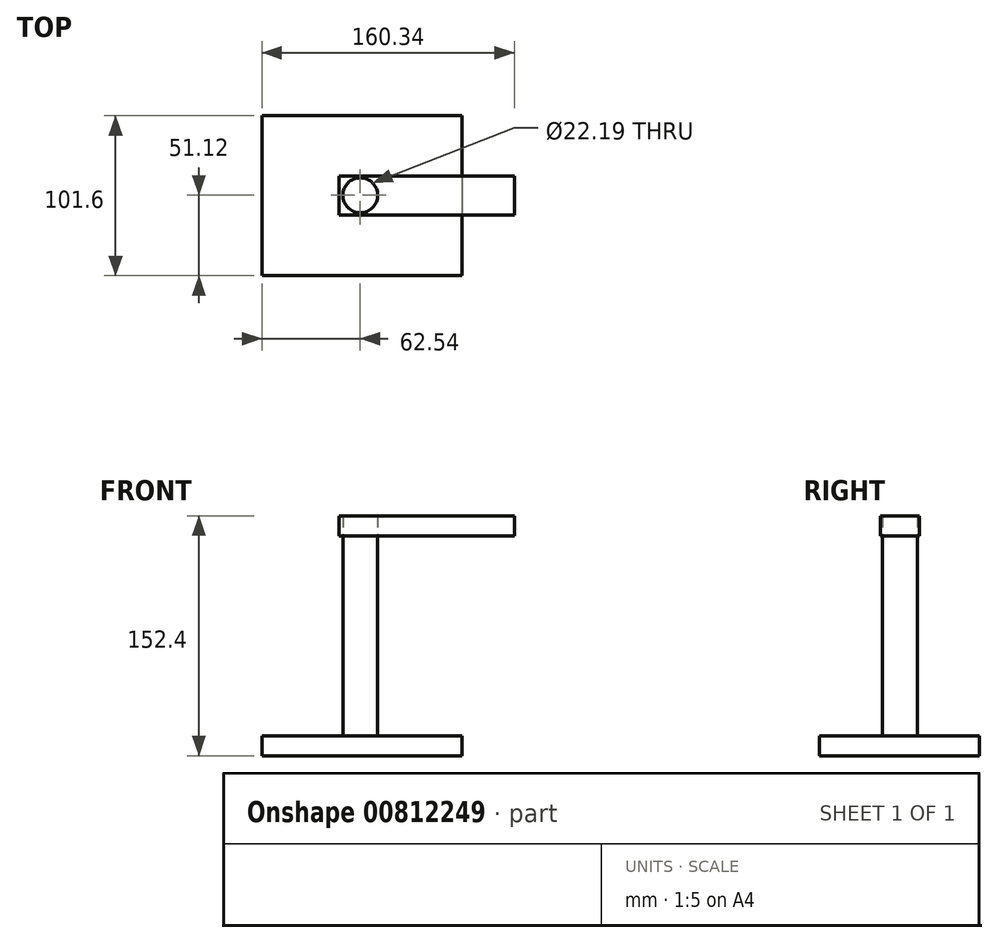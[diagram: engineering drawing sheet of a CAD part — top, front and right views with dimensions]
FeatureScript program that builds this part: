
annotation { "Feature Type Name" : "Feature", "Feature Type Description" : "" }
export const myFeature = defineFeature(function(context is Context, id is Id, definition is map)
    precondition{}
    {
        {
            var Q0;
            Q0=qCreatedBy(makeId("Top.planeOp"),FACE);
            var sketch = newSketch(context, id + "F0", { "sketchPlane" : qUnion([Q0])});
            skLineSegment(sketch, "E0.bottom", {"start": v(-62.54, 50.48) * mm, "end": v(64.46, 50.48) * mm});
            skLineSegment(sketch, "E0.top", {"start": v(-62.54, -51.12) * mm, "end": v(64.46, -51.12) * mm});
            skLineSegment(sketch, "E0.left", {"start": v(-62.54, 50.48) * mm, "end": v(-62.54, -51.12) * mm});
            skLineSegment(sketch, "E0.right", {"start": v(64.46, 50.48) * mm, "end": v(64.46, -51.12) * mm});
            skSolve(sketch);
        }
        {
            var Q0;
            Q0=makeQuery(id+"F0.imprint","IMPRINT",FACE,{"disambiguationData":[TD([[makeQuery(id+"F0.imprint","IMPRINT",EDGE,{"derivedFrom":sQuery(id+"F0.wireOp",EDGE,"E0.bottom")}),-1.0]])]});
            extrude(context, id + "F1", {"entities" : qUnion([Q0]), "depth" : 12.7 * mm, "offsetDistance" : 25.4 * mm});
        }
        {
            var Q0;
            Q0=makeQuery(id+"F1.opExtrude","CAP_FACE",FACE,{"disambiguationData":[OSD([sQuery(id+"F0.wireOp",EDGE,"E0.bottom"),sQuery(id+"F0.wireOp",EDGE,"E0.top"),sQuery(id+"F0.wireOp",EDGE,"E0.left"),sQuery(id+"F0.wireOp",EDGE,"E0.right")])],"isStart":false});
            var sketch = newSketch(context, id + "F2", { "sketchPlane" : qUnion([Q0])});
            skCircle(sketch, "E1", {"center": v(0, 0) * mm, "radius": 11.1 * mm});
            skSolve(sketch);
        }
        {
            var Q0;
            Q0=makeQuery(id+"F2.imprint","IMPRINT",FACE,{"disambiguationData":[TD([[makeQuery(id+"F2.imprint","IMPRINT",EDGE,{"derivedFrom":sQuery(id+"F2.wireOp",EDGE,"E1")}),1.0]])]});
            extrude(context, id + "F3", {"entities" : qUnion([Q0]), "depth" : 127 * mm, "offsetDistance" : 25.4 * mm});
        }
        {
            var Q0;
            Q0=makeQuery(id+"F3.opExtrude","CAP_FACE",FACE,{"disambiguationData":[OSD([sQuery(id+"F2.wireOp",EDGE,"E1")])],"isStart":false});
            var sketch = newSketch(context, id + "F4", { "sketchPlane" : qUnion([Q0])});
            skLineSegment(sketch, "E2.bottom", {"start": v(-13.37, 12.26) * mm, "end": v(97.8, 12.26) * mm});
            skLineSegment(sketch, "E2.top", {"start": v(-13.37, -12.44) * mm, "end": v(97.8, -12.44) * mm});
            skLineSegment(sketch, "E2.left", {"start": v(-13.37, 12.26) * mm, "end": v(-13.37, -12.44) * mm});
            skLineSegment(sketch, "E2.right", {"start": v(97.8, 12.26) * mm, "end": v(97.8, -12.44) * mm});
            skSolve(sketch);
        }
        {
            var Q0;
            Q0=makeQuery(id+"F4.imprint","IMPRINT",FACE,{"disambiguationData":[TD([[makeQuery(id+"F4.imprint","IMPRINT",EDGE,{"derivedFrom":sQuery(id+"F4.wireOp",EDGE,"E2.bottom")}),-1.0]])]});
            extrude(context, id + "F5", {"entities" : qUnion([Q0]), "depth" : 12.7 * mm, "offsetDistance" : 25.4 * mm});
        }
    });
